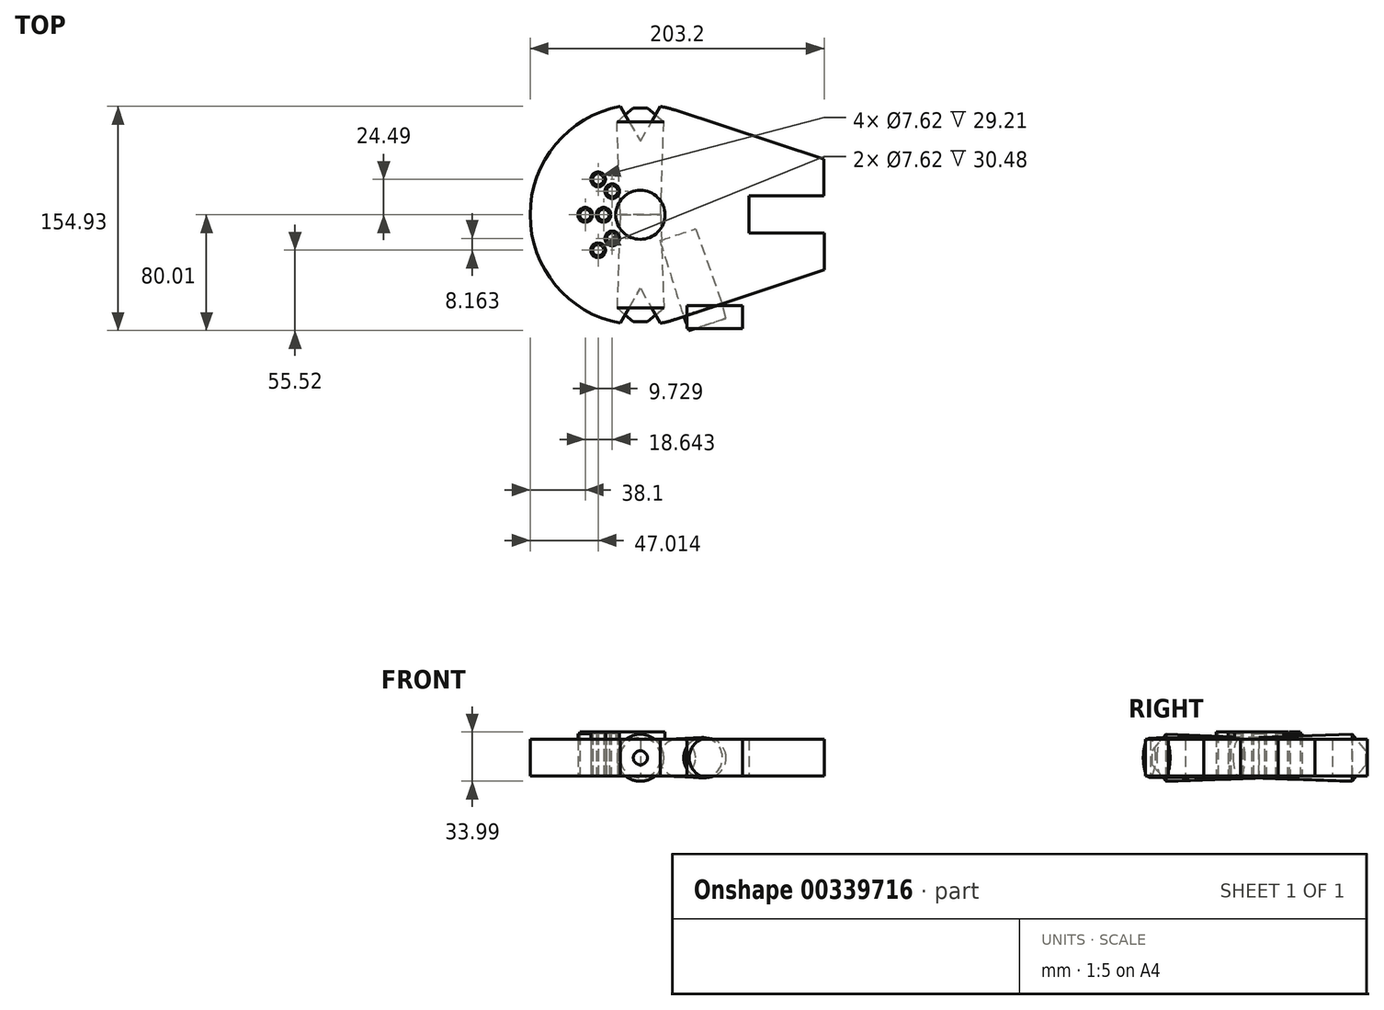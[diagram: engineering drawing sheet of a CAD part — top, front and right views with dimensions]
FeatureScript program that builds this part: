
annotation { "Feature Type Name" : "Feature", "Feature Type Description" : "" }
export const myFeature = defineFeature(function(context is Context, id is Id, definition is map)
    precondition{}
    {
        {
            var Q0;
            Q0=qCreatedBy(makeId("Top.planeOp"),FACE);
            var sketch = newSketch(context, id + "F0", { "sketchPlane" : qUnion([Q0])});
            skArc(sketch, "E0", {"start": v(75.06, 13.13) * mm, "mid": v(54.17, 53.6) * mm, "end": v(13.92, 74.92) * mm});
            skLineSegment(sketch, "E1.0", {"start": v(75.13, -12.7) * mm, "end": v(127, -12.7) * mm});
            skLineSegment(sketch, "E2.0", {"start": v(75.06, 13.13) * mm, "end": v(126.87, 13.13) * mm});
            skLineSegment(sketch, "E3", {"start": v(127, -12.7) * mm, "end": v(127, -38.1) * mm});
            skLineSegment(sketch, "E4", {"start": v(126.87, 13.13) * mm, "end": v(126.87, 38.53) * mm});
            skLineSegment(sketch, "E5", {"start": v(126.87, 38.53) * mm, "end": v(23.78, 72.4) * mm});
            skLineSegment(sketch, "E6", {"start": v(127, -38.1) * mm, "end": v(23.78, -72.4) * mm});
            skPoint(sketch, "E7.start.orphan", {"position": v(0, -76.2) * mm});
            skLineSegment(sketch, "E8", {"start": v(75.06, 13.13) * mm, "end": v(75.13, -12.7) * mm});
            skLineSegment(sketch, "E9", {"start": v(0, 50.8) * mm, "end": v(13.92, 74.92) * mm});
            skLineSegment(sketch, "E10", {"start": v(-13.92, 74.92) * mm, "end": v(0, 50.8) * mm});
            skArc(sketch, "E11.trimOffspring", {"start": v(-13.92, 74.92) * mm, "mid": v(-76.2, 0) * mm, "end": v(-13.92, -74.92) * mm});
            skPoint(sketch, "E12.orphan", {"position": v(0, 76.2) * mm});
            skLineSegment(sketch, "E13.MirrorCS", {"start": v(0, -50.8) * mm, "end": v(13.92, -74.92) * mm});
            skLineSegment(sketch, "E14.MirrorCS", {"start": v(-13.92, -74.92) * mm, "end": v(0, -50.8) * mm});
            skArc(sketch, "E15.trimOffspring", {"start": v(13.92, -74.92) * mm, "mid": v(54.32, -53.44) * mm, "end": v(75.13, -12.7) * mm});
            skSolve(sketch);
        }
        {
            var Q0;
            Q0 = qSketchRegion(id + "F0", true);
            extrude(context, id + "F1", {"entities" : qUnion([Q0]), "depth" : 25.4 * mm});
        }
        {
            var Q0;
            Q0=qCreatedBy(makeId("Top.planeOp"),FACE);
            var sketch = newSketch(context, id + "F2", { "sketchPlane" : qUnion([Q0])});
            skCircle(sketch, "E16", {"center": v(0, 0) * mm, "radius": 16.94 * mm});
            skSolve(sketch);
        }
        {
            var Q0;
            Q0 = qSketchRegion(id + "F2", true);
            extrude(context, id + "F3", {"entities" : qUnion([Q0]), "operationType" : NewBodyOperationType.ADD, "depth" : 30.48 * mm, "offsetDistance" : 25.4 * mm});
        }
        {
            var Q0;
            Q0=qCreatedBy(makeId("Top.planeOp"),FACE);
            var sketch = newSketch(context, id + "F4", { "sketchPlane" : qUnion([Q0])});
            skPoint(sketch, "E17.orphan", {"position": v(-29.19, 0) * mm});
            skPoint(sketch, "E18.end.orphan", {"position": v(-19.46, 0) * mm});
            skCircle(sketch, "E19", {"center": v(-19.46, 16.33) * mm, "radius": 3.81 * mm});
            skCircle(sketch, "E20", {"center": v(-29.19, 24.5) * mm, "radius": 5.08 * mm});
            skCircle(sketch, "E21", {"center": v(-19.46, 16.33) * mm, "radius": 5.08 * mm});
            skCircle(sketch, "E22", {"center": v(-29.19, 24.5) * mm, "radius": 3.81 * mm});
            skCircle(sketch, "E23.MirrorC", {"center": v(-19.46, -16.33) * mm, "radius": 3.81 * mm});
            skCircle(sketch, "E24.MirrorC", {"center": v(-19.46, -16.33) * mm, "radius": 5.08 * mm});
            skCircle(sketch, "E25.MirrorC", {"center": v(-29.19, -24.5) * mm, "radius": 5.08 * mm});
            skCircle(sketch, "E26.MirrorC", {"center": v(-29.19, -24.5) * mm, "radius": 3.81 * mm});
            skCircle(sketch, "E27", {"center": v(-25.4, 0) * mm, "radius": 3.81 * mm});
            skCircle(sketch, "E28", {"center": v(-25.4, 0) * mm, "radius": 5.08 * mm});
            skCircle(sketch, "E29", {"center": v(-38.1, 0) * mm, "radius": 3.81 * mm});
            skCircle(sketch, "E30", {"center": v(-38.1, 0) * mm, "radius": 5.08 * mm});
            skLineSegment(sketch, "E31.trimOffspring", {"start": v(-29.19, 0) * mm, "end": v(-29.21, 0) * mm});
            skSolve(sketch);
        }
        {
            var Q0;
            Q0=makeQuery(id+"F4.imprint","IMPRINT",FACE,{"disambiguationData":[TD([[makeQuery(id+"F4.imprint","IMPRINT",EDGE,{"derivedFrom":sQuery(id+"F4.wireOp",EDGE,"E19")}),1.0]])]});
            var Q1;
            Q1=makeQuery(id+"F4.imprint","IMPRINT",FACE,{"disambiguationData":[TD([[makeQuery(id+"F4.imprint","IMPRINT",EDGE,{"derivedFrom":sQuery(id+"F4.wireOp",EDGE,"E22")}),1.0]])]});
            var Q2;
            Q2=makeQuery(id+"F4.imprint","IMPRINT",FACE,{"disambiguationData":[TD([[makeQuery(id+"F4.imprint","IMPRINT",EDGE,{"derivedFrom":sQuery(id+"F4.wireOp",EDGE,"E29")}),1.0]])]});
            var Q3;
            Q3=makeQuery(id+"F4.imprint","IMPRINT",FACE,{"disambiguationData":[TD([[makeQuery(id+"F4.imprint","IMPRINT",EDGE,{"derivedFrom":sQuery(id+"F4.wireOp",EDGE,"E27")}),1.0]])]});
            var Q4;
            Q4=makeQuery(id+"F4.imprint","IMPRINT",FACE,{"disambiguationData":[TD([[makeQuery(id+"F4.imprint","IMPRINT",EDGE,{"derivedFrom":sQuery(id+"F4.wireOp",EDGE,"E23.MirrorC")}),-1.0]])]});
            var Q5;
            Q5=makeQuery(id+"F4.imprint","IMPRINT",FACE,{"disambiguationData":[TD([[makeQuery(id+"F4.imprint","IMPRINT",EDGE,{"derivedFrom":sQuery(id+"F4.wireOp",EDGE,"E26.MirrorC")}),-1.0]])]});
            extrude(context, id + "F5", {"entities" : qUnion([Q0, Q1, Q2, Q3, Q4, Q5]), "depth" : 30.48 * mm, "offsetDistance" : 25.4 * mm});
        }
        {
            var Q0;
            Q0=makeQuery(id+"F4.imprint","IMPRINT",FACE,{"disambiguationData":[TD([[makeQuery(id+"F4.imprint","IMPRINT",EDGE,{"derivedFrom":sQuery(id+"F4.wireOp",EDGE,"E25.MirrorC")}),-1.0]])]});
            var Q1;
            Q1=makeQuery(id+"F4.imprint","IMPRINT",FACE,{"disambiguationData":[TD([[makeQuery(id+"F4.imprint","IMPRINT",EDGE,{"derivedFrom":sQuery(id+"F4.wireOp",EDGE,"E23.MirrorC")}),1.0]])]});
            var Q2;
            Q2=makeQuery(id+"F4.imprint","IMPRINT",FACE,{"disambiguationData":[TD([[makeQuery(id+"F4.imprint","IMPRINT",EDGE,{"derivedFrom":sQuery(id+"F4.wireOp",EDGE,"E27")}),-1.0]])]});
            var Q3;
            Q3=makeQuery(id+"F4.imprint","IMPRINT",FACE,{"disambiguationData":[TD([[makeQuery(id+"F4.imprint","IMPRINT",EDGE,{"derivedFrom":sQuery(id+"F4.wireOp",EDGE,"E29")}),-1.0]])]});
            var Q4;
            Q4=makeQuery(id+"F4.imprint","IMPRINT",FACE,{"disambiguationData":[TD([[makeQuery(id+"F4.imprint","IMPRINT",EDGE,{"derivedFrom":sQuery(id+"F4.wireOp",EDGE,"E19")}),-1.0]])]});
            var Q5;
            Q5=makeQuery(id+"F4.imprint","IMPRINT",FACE,{"disambiguationData":[TD([[makeQuery(id+"F4.imprint","IMPRINT",EDGE,{"derivedFrom":sQuery(id+"F4.wireOp",EDGE,"E20")}),1.0]])]});
            extrude(context, id + "F6", {"entities" : qUnion([Q0, Q1, Q2, Q3, Q4, Q5]), "depth" : 29.2 * mm, "offsetDistance" : 25.4 * mm});
        }
        {
            var Q0;
            Q0=qCreatedBy(makeId("Front.planeOp"),FACE);
            var sketch = newSketch(context, id + "F7", { "sketchPlane" : qUnion([Q0])});
            skCircle(sketch, "E32", {"center": v(0, 12.7) * mm, "radius": 13.97 * mm});
            skSolve(sketch);
        }
        {
            var Q0;
            Q0 = qSketchRegion(id + "F7", true);
            extrude(context, id + "F8", {"entities" : qUnion([Q0]), "depth" : 64.28 * mm, "offsetDistance" : 25.4 * mm, "hasDraft" : true, "draftAngle" : 2 * degree, "hasSecondDirection" : true, "secondDirectionOppositeDirection" : true, "secondDirectionDepth" : 64.3 * mm, "hasSecondDirectionDraft" : true, "secondDirectionDraftAngle" : 2 * degree});
        }
        {
            var Q0;
            Q0=makeQuery(id+"F8.opExtrude","CAP_FACE",FACE,{"disambiguationData":[OSD([sQuery(id+"F7.wireOp",EDGE,"E32")])],"isStart":false});
            var sketch = newSketch(context, id + "F9", { "sketchPlane" : qUnion([Q0])});
            skCircle(sketch, "E33", {"center": v(0, 12.7) * mm, "radius": 16.34 * mm});
            skSolve(sketch);
        }
        {
            var Q0;
            Q0=makeQuery(id+"F9.imprint","IMPRINT",FACE,{"disambiguationData":[TD([[makeQuery(id+"F9.imprint","IMPRINT",EDGE,{"derivedFrom":makeQuery(id+"F8.opExtrude","CAP_EDGE",EDGE,{"disambiguationData":[OSD([sQuery(id+"F7.wireOp",EDGE,"E32")])],"isStart":false})}),1.0]])]});
            var Q1;
            Q1=sQuery(id+"F9.wireOp",EDGE,"E33");
            extrude(context, id + "F10", {"entities" : qUnion([Q0]), "surfaceEntities" : qUnion([Q1]), "depth" : 9.52 * mm, "offsetDistance" : 25.4 * mm, "hasDraft" : true, "draftAngle" : 50 * degree, "draftPullDirection" : true, "hasSecondDirectionDraft" : true, "secondDirectionDraftAngle" : 50 * degree, "secondDirectionDraftPullDirection" : true});
        }
        {
            var Q0;
            Q0=makeQuery(id+"F10.opExtrude","SWEPT_BODY",BODY,{"disambiguationData":[OSD([sQuery(id+"F7.wireOp",EDGE,"E32")])]});
            var Q1;
            Q1=qCreatedBy(makeId("Front.planeOp"),FACE);
            mirror(context, id + "F11", {"entities" : qUnion([Q0]), "mirrorPlane" : qUnion([Q1])});
        }
        {
            var Q0;
            Q0=makeQuery(id+"F1.opExtrude","SWEPT_FACE",FACE,{"disambiguationData":[OSD([sQuery(id+"F0.wireOp",EDGE,"E6")])]});
            cPlane(context, id + "F12", {"entities" : qUnion([Q0]), "cplaneType" : CPlaneType.OFFSET, "offset" : 0 * mm, "width" : 152.4 * mm, "height" : 152.4 * mm});
        }
        {
            var Q0;
            Q0=qCreatedBy(id+"F12.planeOp",FACE);
            var sketch = newSketch(context, id + "F13", { "sketchPlane" : qUnion([Q0])});
            skCircle(sketch, "E34", {"center": v(20.2, 12.7) * mm, "radius": 13.97 * mm});
            skSolve(sketch);
        }
        {
            var Q0;
            Q0 = qSketchRegion(id + "F13", true);
            extrude(context, id + "F14", {"entities" : qUnion([Q0]), "oppositeDirection" : true, "depth" : 55.03 * mm, "offsetDistance" : 25.4 * mm, "hasDraft" : true, "draftAngle" : 1 * degree, "draftPullDirection" : true, "hasSecondDirection" : true, "secondDirectionOppositeDirection" : false, "secondDirectionDepth" : 10.36 * mm, "hasSecondDirectionDraft" : true, "secondDirectionDraftAngle" : 3 * degree, "secondDirectionDraftPullDirection" : true});
        }
        {
            var Q0;
            Q0=qCreatedBy(makeId("Top.planeOp"),FACE);
            var sketch = newSketch(context, id + "F15", { "sketchPlane" : qUnion([Q0])});
            skLineSegment(sketch, "E35.bottom", {"start": v(32.16, -78.5) * mm, "end": v(70.59, -78.5) * mm});
            skLineSegment(sketch, "E35.top", {"start": v(32.16, -62.7) * mm, "end": v(70.59, -62.7) * mm});
            skLineSegment(sketch, "E35.left", {"start": v(32.16, -78.5) * mm, "end": v(32.16, -62.7) * mm});
            skLineSegment(sketch, "E35.right", {"start": v(70.59, -78.5) * mm, "end": v(70.59, -62.7) * mm});
            skSolve(sketch);
        }
        {
            var Q0;
            Q0 = qSketchRegion(id + "F15", true);
            extrude(context, id + "F16", {"entities" : qUnion([Q0]), "depth" : 25.4 * mm, "offsetDistance" : 25.4 * mm});
        }
    });
